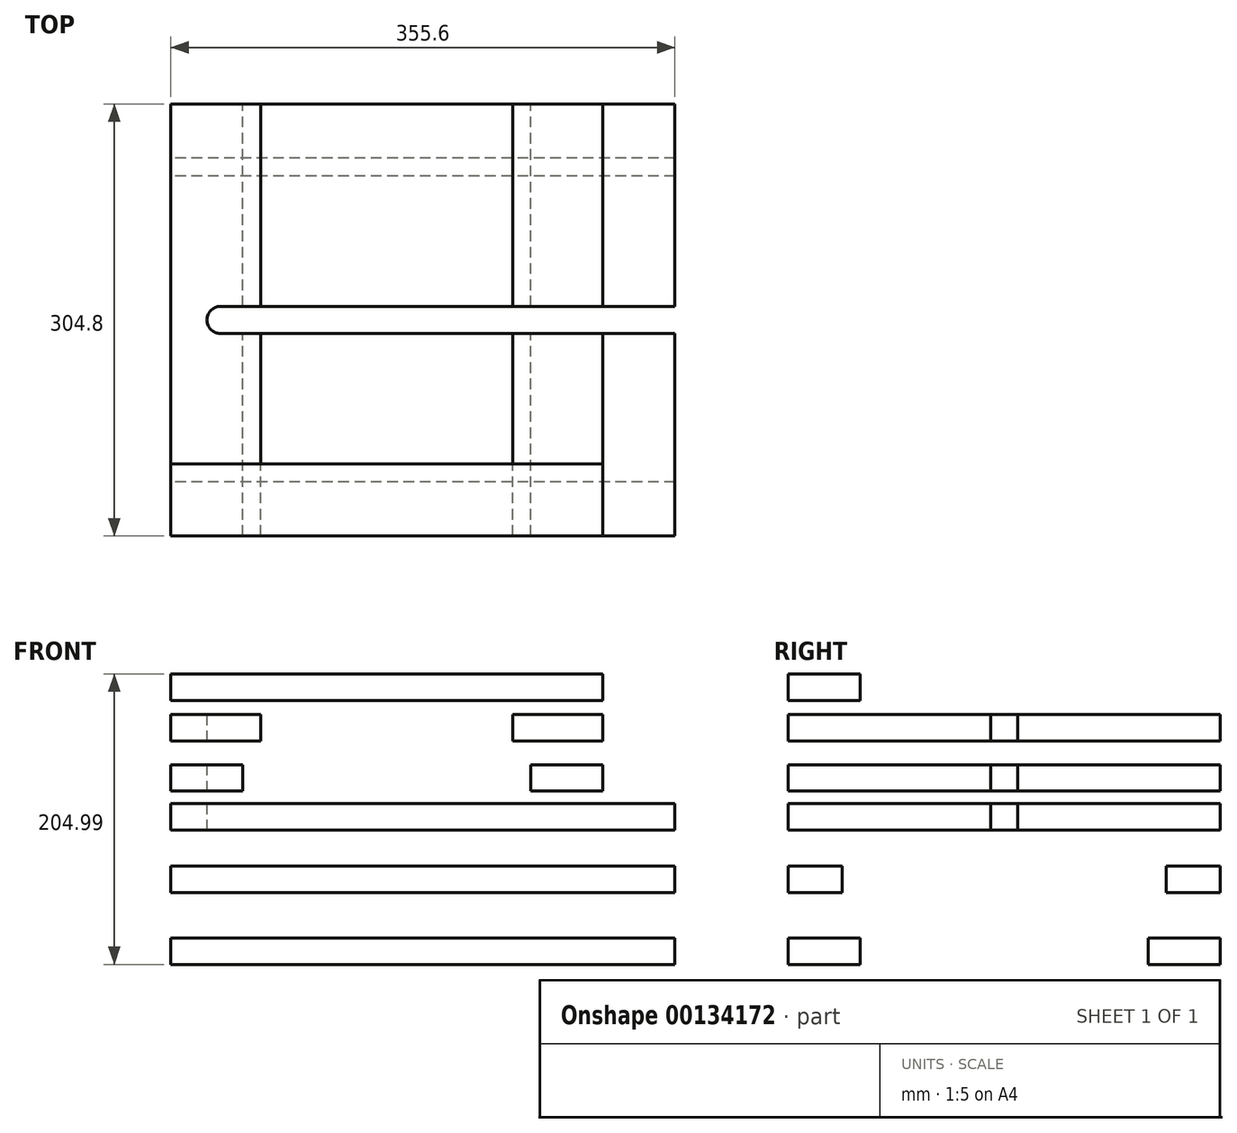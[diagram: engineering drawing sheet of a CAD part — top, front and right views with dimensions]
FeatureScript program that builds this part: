
annotation { "Feature Type Name" : "Feature", "Feature Type Description" : "" }
export const myFeature = defineFeature(function(context is Context, id is Id, definition is map)
    precondition{}
    {
        {
            var Q0;
            Q0=qCreatedBy(makeId("Front.planeOp"),FACE);
            var sketch = newSketch(context, id + "F0", { "sketchPlane" : qUnion([Q0])});
            skLineSegment(sketch, "E0.bottom", {"start": v(-177.8, -9.32) * mm, "end": v(177.8, -9.32) * mm});
            skLineSegment(sketch, "E0.top", {"start": v(-177.8, 9.32) * mm, "end": v(177.8, 9.32) * mm});
            skLineSegment(sketch, "E0.left", {"start": v(-177.8, -9.32) * mm, "end": v(-177.8, 9.32) * mm});
            skLineSegment(sketch, "E0.right", {"start": v(177.8, -9.32) * mm, "end": v(177.8, 9.32) * mm});
            skPoint(sketch, "E0.middle", {"position": v(0, 0) * mm});
            skLineSegment(sketch, "E1.bottom", {"start": v(-177.8, 36.83) * mm, "end": v(-127, 36.83) * mm});
            skLineSegment(sketch, "E1.top", {"start": v(-177.8, 18.18) * mm, "end": v(-127, 18.18) * mm});
            skLineSegment(sketch, "E1.left", {"start": v(-177.8, 36.83) * mm, "end": v(-177.8, 18.18) * mm});
            skLineSegment(sketch, "E1.right", {"start": v(-127, 36.83) * mm, "end": v(-127, 18.18) * mm});
            skLineSegment(sketch, "E2.bottom", {"start": v(76.2, 18.18) * mm, "end": v(127, 18.18) * mm});
            skLineSegment(sketch, "E2.top", {"start": v(76.2, 36.83) * mm, "end": v(127, 36.83) * mm});
            skLineSegment(sketch, "E2.left", {"start": v(76.2, 18.18) * mm, "end": v(76.2, 36.83) * mm});
            skLineSegment(sketch, "E2.right", {"start": v(127, 18.18) * mm, "end": v(127, 36.83) * mm});
            skLineSegment(sketch, "E3.bottom", {"start": v(-177.8, 53.61) * mm, "end": v(-114.3, 53.61) * mm});
            skLineSegment(sketch, "E3.top", {"start": v(-177.8, 72.26) * mm, "end": v(-114.3, 72.26) * mm});
            skLineSegment(sketch, "E3.left", {"start": v(-177.8, 53.61) * mm, "end": v(-177.8, 72.26) * mm});
            skLineSegment(sketch, "E3.right", {"start": v(-114.3, 53.61) * mm, "end": v(-114.3, 72.26) * mm});
            skLineSegment(sketch, "E4.bottom", {"start": v(63.5, 53.61) * mm, "end": v(127, 53.61) * mm});
            skLineSegment(sketch, "E4.top", {"start": v(63.5, 72.26) * mm, "end": v(127, 72.26) * mm});
            skLineSegment(sketch, "E4.left", {"start": v(63.5, 53.61) * mm, "end": v(63.5, 72.26) * mm});
            skLineSegment(sketch, "E4.right", {"start": v(127, 53.61) * mm, "end": v(127, 72.26) * mm});
            skSolve(sketch);
        }
        {
            var Q0;
            Q0=makeQuery(id+"F0.imprint","IMPRINT",FACE,{"disambiguationData":[TD([[makeQuery(id+"F0.imprint","IMPRINT",EDGE,{"derivedFrom":sQuery(id+"F0.wireOp",EDGE,"E3.bottom")}),1.0]])]});
            var Q1;
            Q1=makeQuery(id+"F0.imprint","IMPRINT",FACE,{"disambiguationData":[TD([[makeQuery(id+"F0.imprint","IMPRINT",EDGE,{"derivedFrom":sQuery(id+"F0.wireOp",EDGE,"E1.bottom")}),-1.0]])]});
            var Q2;
            Q2=makeQuery(id+"F0.imprint","IMPRINT",FACE,{"disambiguationData":[TD([[makeQuery(id+"F0.imprint","IMPRINT",EDGE,{"derivedFrom":sQuery(id+"F0.wireOp",EDGE,"E0.bottom")}),1.0]])]});
            var Q3;
            Q3=makeQuery(id+"F0.imprint","IMPRINT",FACE,{"disambiguationData":[TD([[makeQuery(id+"F0.imprint","IMPRINT",EDGE,{"derivedFrom":sQuery(id+"F0.wireOp",EDGE,"E2.bottom")}),1.0]])]});
            var Q4;
            Q4=makeQuery(id+"F0.imprint","IMPRINT",FACE,{"disambiguationData":[TD([[makeQuery(id+"F0.imprint","IMPRINT",EDGE,{"derivedFrom":sQuery(id+"F0.wireOp",EDGE,"E4.bottom")}),1.0]])]});
            extrude(context, id + "F1", {"entities" : qUnion([Q0, Q1, Q2, Q3, Q4]), "depth" : 304.8 * mm});
        }
        {
            var Q0;
            Q0=makeQuery(id+"F1.opExtrude","SWEPT_FACE",FACE,{"disambiguationData":[OSD([sQuery(id+"F0.wireOp",EDGE,"E0.bottom")])]});
            var sketch = newSketch(context, id + "F2", { "sketchPlane" : qUnion([Q0])});
            skArc(sketch, "E5", {"start": v(-142.88, 161.93) * mm, "mid": v(-152.4, 152.4) * mm, "end": v(-142.88, 142.88) * mm});
            skPoint(sketch, "E5.centerSnap0", {"position": v(-177.8, 152.4) * mm});
            skLineSegment(sketch, "E6", {"start": v(-142.88, 161.93) * mm, "end": v(177.8, 161.93) * mm});
            skLineSegment(sketch, "E7", {"start": v(-142.87, 142.88) * mm, "end": v(177.8, 142.88) * mm});
            skLineSegment(sketch, "E8", {"start": v(177.8, 142.88) * mm, "end": v(-142.88, 142.88) * mm});
            skSolve(sketch);
        }
        {
            var Q0;
            Q0=makeQuery(id+"F2.imprint","IMPRINT",FACE,{"disambiguationData":[TD([[makeQuery(id+"F2.imprint","IMPRINT",EDGE,{"derivedFrom":sQuery(id+"F2.wireOp",EDGE,"E5")}),1.0]])]});
            extrude(context, id + "F3", {"entities" : qUnion([Q0]), "operationType" : NewBodyOperationType.REMOVE, "endBound" : BoundingType.THROUGH_ALL, "oppositeDirection" : true, "depth" : 25.4 * mm});
        }
        {
            var Q0;
            Q0=qCreatedBy(makeId("Right.planeOp"),FACE);
            var sketch = newSketch(context, id + "F4", { "sketchPlane" : qUnion([Q0])});
            skLineSegment(sketch, "E9.bottom", {"start": v(-50.8, -104.17) * mm, "end": v(0, -104.17) * mm});
            skLineSegment(sketch, "E9.top", {"start": v(-50.8, -85.52) * mm, "end": v(0, -85.52) * mm});
            skLineSegment(sketch, "E9.left", {"start": v(-50.8, -104.17) * mm, "end": v(-50.8, -85.52) * mm});
            skLineSegment(sketch, "E9.right", {"start": v(0, -104.17) * mm, "end": v(0, -85.52) * mm});
            skLineSegment(sketch, "E10.bottom", {"start": v(-304.8, -85.52) * mm, "end": v(-254, -85.52) * mm});
            skLineSegment(sketch, "E10.top", {"start": v(-304.8, -104.17) * mm, "end": v(-254, -104.17) * mm});
            skLineSegment(sketch, "E10.left", {"start": v(-254, -85.52) * mm, "end": v(-254, -104.17) * mm});
            skLineSegment(sketch, "E10.right", {"start": v(-304.8, -85.52) * mm, "end": v(-304.8, -104.17) * mm});
            skLineSegment(sketch, "E11.bottom", {"start": v(-304.8, -53.37) * mm, "end": v(-266.7, -53.37) * mm});
            skLineSegment(sketch, "E11.top", {"start": v(-304.8, -34.72) * mm, "end": v(-266.7, -34.72) * mm});
            skLineSegment(sketch, "E11.left", {"start": v(-304.8, -53.37) * mm, "end": v(-304.8, -34.72) * mm});
            skLineSegment(sketch, "E11.right", {"start": v(-266.7, -53.37) * mm, "end": v(-266.7, -34.72) * mm});
            skLineSegment(sketch, "E12.bottom", {"start": v(0, -34.72) * mm, "end": v(-38.1, -34.72) * mm});
            skLineSegment(sketch, "E12.top", {"start": v(0, -53.37) * mm, "end": v(-38.1, -53.37) * mm});
            skLineSegment(sketch, "E12.left", {"start": v(0, -34.72) * mm, "end": v(0, -53.37) * mm});
            skLineSegment(sketch, "E12.right", {"start": v(-38.1, -34.72) * mm, "end": v(-38.1, -53.37) * mm});
            skSolve(sketch);
        }
        {
            var Q0;
            Q0 = qSketchRegion(id + "F4", true);
            extrude(context, id + "F5", {"entities" : qUnion([Q0]), "endBound" : BoundingType.SYMMETRIC, "depth" : 355.6 * mm});
        }
        {
            var Q0;
            Q0=qCreatedBy(makeId("Right.planeOp"),FACE);
            var sketch = newSketch(context, id + "F6", { "sketchPlane" : qUnion([Q0])});
            skLineSegment(sketch, "E13.bottom", {"start": v(-304.8, 82.17) * mm, "end": v(-254, 82.17) * mm});
            skLineSegment(sketch, "E13.top", {"start": v(-304.8, 100.82) * mm, "end": v(-254, 100.82) * mm});
            skLineSegment(sketch, "E13.left", {"start": v(-304.8, 82.17) * mm, "end": v(-304.8, 100.82) * mm});
            skLineSegment(sketch, "E13.right", {"start": v(-254, 82.17) * mm, "end": v(-254, 100.82) * mm});
            skSolve(sketch);
        }
        {
            var Q0;
            Q0=makeQuery(id+"F6.imprint","IMPRINT",FACE,{"disambiguationData":[TD([[makeQuery(id+"F6.imprint","IMPRINT",EDGE,{"derivedFrom":sQuery(id+"F6.wireOp",EDGE,"E13.bottom")}),1.0]])]});
            extrude(context, id + "F7", {"entities" : qUnion([Q0]), "depth" : 127 * mm, "hasSecondDirection" : true, "secondDirectionOppositeDirection" : true, "secondDirectionDepth" : 177.8 * mm});
        }
    });
